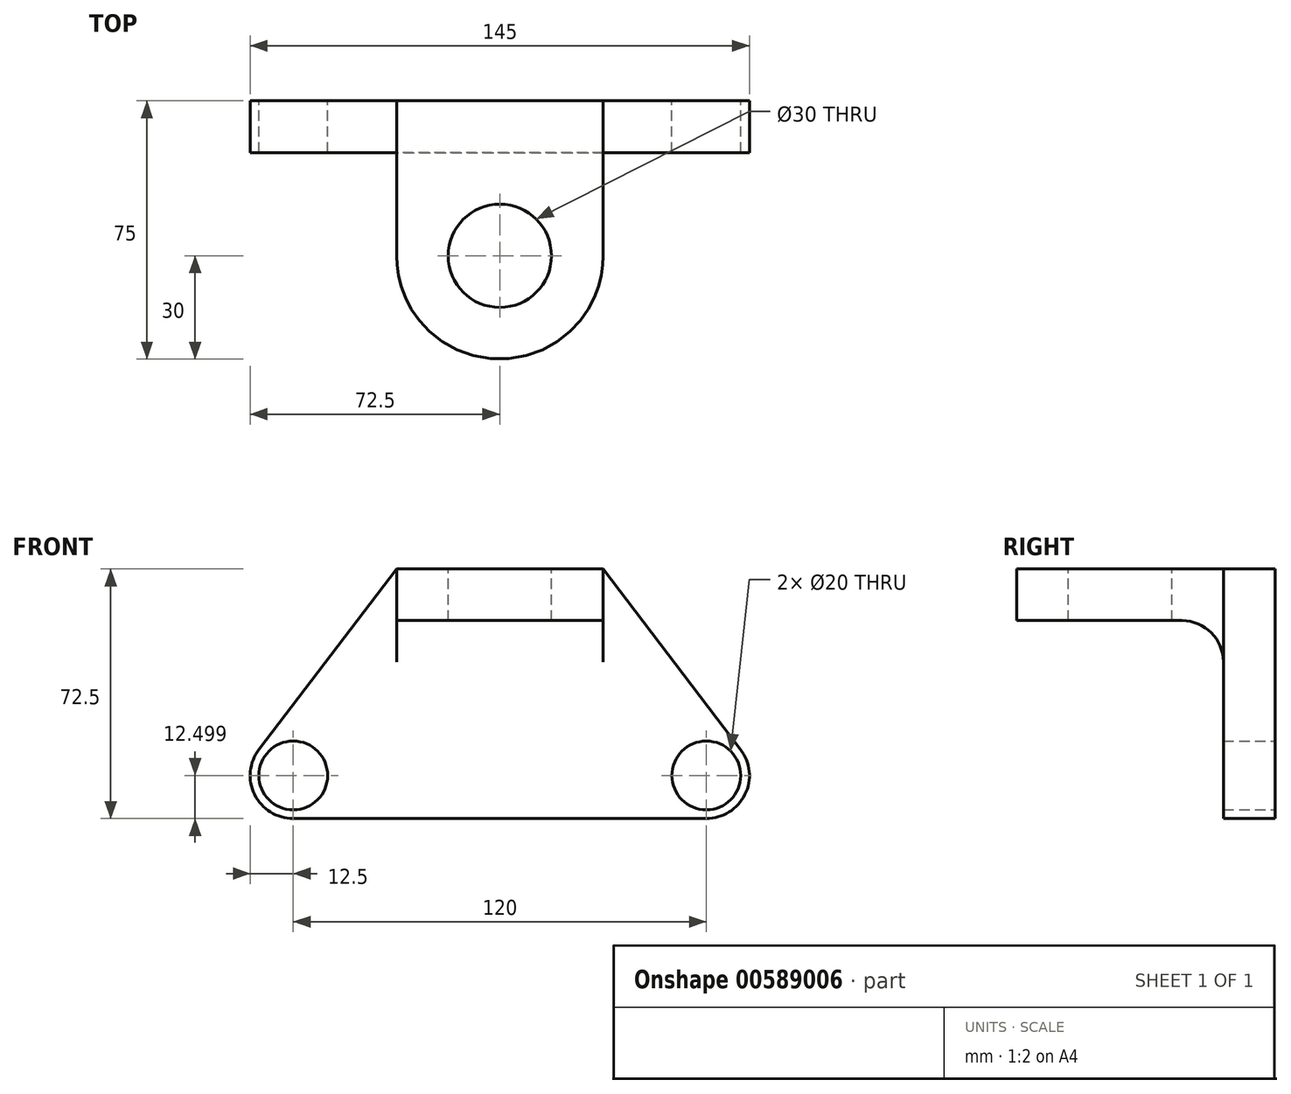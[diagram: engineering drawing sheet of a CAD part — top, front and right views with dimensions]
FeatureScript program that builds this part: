
annotation { "Feature Type Name" : "Feature", "Feature Type Description" : "" }
export const myFeature = defineFeature(function(context is Context, id is Id, definition is map)
    precondition{}
    {
        {
            var Q0;
            Q0=qCreatedBy(makeId("Front.planeOp"),FACE);
            var sketch = newSketch(context, id + "F0", { "sketchPlane" : qUnion([Q0])});
            skLineSegment(sketch, "E0", {"start": v(0, 82.26) * mm, "end": v(0, -96.92) * mm, "construction": true});
            skLineSegment(sketch, "E1", {"start": v(0, -35) * mm, "end": v(-60, -35) * mm, "construction": true});
            skCircle(sketch, "E2", {"center": v(-60, -35) * mm, "radius": 10 * mm});
            skArc(sketch, "E3", {"start": v(-69.94, -27.42) * mm, "mid": v(-71.2, -40.55) * mm, "end": v(-60, -47.5) * mm});
            skLineSegment(sketch, "E4.MirrorCS", {"start": v(0, -35) * mm, "end": v(60, -35) * mm, "construction": true});
            skCircle(sketch, "E5.MirrorC", {"center": v(60, -35) * mm, "radius": 10 * mm});
            skArc(sketch, "E6.MirrorC", {"start": v(69.94, -27.42) * mm, "mid": v(71.2, -40.55) * mm, "end": v(60, -47.5) * mm});
            skLineSegment(sketch, "E7", {"start": v(-60, -47.5) * mm, "end": v(60, -47.5) * mm});
            skLineSegment(sketch, "E8", {"start": v(0, 25) * mm, "end": v(-30, 25) * mm});
            skLineSegment(sketch, "E9", {"start": v(0, 25) * mm, "end": v(30, 25) * mm});
            skLineSegment(sketch, "E10", {"start": v(-30, 25) * mm, "end": v(-69.94, -27.42) * mm});
            skLineSegment(sketch, "E11.MirrorCS", {"start": v(30, 25) * mm, "end": v(69.94, -27.42) * mm});
            skSolve(sketch);
        }
        {
            var Q0;
            Q0 = qSketchRegion(id + "F0", true);
            extrude(context, id + "F1", {"entities" : qUnion([Q0]), "depth" : 15 * mm, "offsetDistance" : 25 * mm});
        }
        {
            var Q0;
            Q0=makeQuery(id+"F1.opExtrude","SWEPT_FACE",FACE,{"disambiguationData":[OSD([sQuery(id+"F0.wireOp",EDGE,"E8"),sQuery(id+"F0.wireOp",EDGE,"E9")])]});
            cPlane(context, id + "F2", {"entities" : qUnion([Q0]), "cplaneType" : CPlaneType.OFFSET, "offset" : 0 * mm, "oppositeDirection" : true, "width" : 150 * mm, "height" : 150 * mm});
        }
        {
            var Q0;
            Q0=qCreatedBy(id+"F2.planeOp",FACE);
            var sketch = newSketch(context, id + "F3", { "sketchPlane" : qUnion([Q0])});
            skLineSegment(sketch, "E12", {"start": v(0, 0) * mm, "end": v(0, -45) * mm, "construction": true});
            skCircle(sketch, "E13", {"center": v(0, -45) * mm, "radius": 15 * mm});
            skArc(sketch, "E14", {"start": v(-30, -45) * mm, "mid": v(0, -75) * mm, "end": v(30, -45) * mm});
            skLineSegment(sketch, "E15", {"start": v(-30, -15) * mm, "end": v(-30, -45) * mm});
            skLineSegment(sketch, "E16.MirrorCS", {"start": v(30, -15) * mm, "end": v(30, -45) * mm});
            skLineSegment(sketch, "E17", {"start": v(-30, -15) * mm, "end": v(-30, 0) * mm});
            skLineSegment(sketch, "E18", {"start": v(-30, 0) * mm, "end": v(30, 0) * mm});
            skLineSegment(sketch, "E19", {"start": v(30, 0) * mm, "end": v(30, -15) * mm});
            skSolve(sketch);
        }
        {
            var Q0;
            Q0 = qSketchRegion(id + "F3", true);
            extrude(context, id + "F4", {"entities" : qUnion([Q0]), "operationType" : NewBodyOperationType.ADD, "oppositeDirection" : true, "depth" : 15 * mm, "offsetDistance" : 25 * mm});
        }
        {
            var Q0;
            Q0=makeQuery(id+"F4.boolean.opBoolean","INTERSECT",EDGE,{"derivedFrom":[makeQuery(id+"F1.opExtrude","CAP_FACE",FACE,{"disambiguationData":[OSD([sQuery(id+"F0.wireOp",EDGE,"E2"),sQuery(id+"F0.wireOp",EDGE,"E3"),sQuery(id+"F0.wireOp",EDGE,"E5.MirrorC"),sQuery(id+"F0.wireOp",EDGE,"E6.MirrorC"),sQuery(id+"F0.wireOp",EDGE,"E7"),sQuery(id+"F0.wireOp",EDGE,"E8"),sQuery(id+"F0.wireOp",EDGE,"E9"),sQuery(id+"F0.wireOp",EDGE,"E10"),sQuery(id+"F0.wireOp",EDGE,"E11.MirrorCS")])],"isStart":false}),makeQuery(id+"F4.opExtrude","CAP_FACE",FACE,{"disambiguationData":[OSD([sQuery(id+"F3.wireOp",EDGE,"E13"),sQuery(id+"F3.wireOp",EDGE,"E14"),sQuery(id+"F3.wireOp",EDGE,"E15"),sQuery(id+"F3.wireOp",EDGE,"E16.MirrorCS"),sQuery(id+"F3.wireOp",EDGE,"E17"),sQuery(id+"F3.wireOp",EDGE,"E18"),sQuery(id+"F3.wireOp",EDGE,"E19")])],"isStart":false})]});
            fillet(context, id + "F5", {"entities" : qUnion([Q0]), "radius" : 12 * mm, "tangentPropagation" : true, "allowEdgeOverflow" : false});
        }
    });
